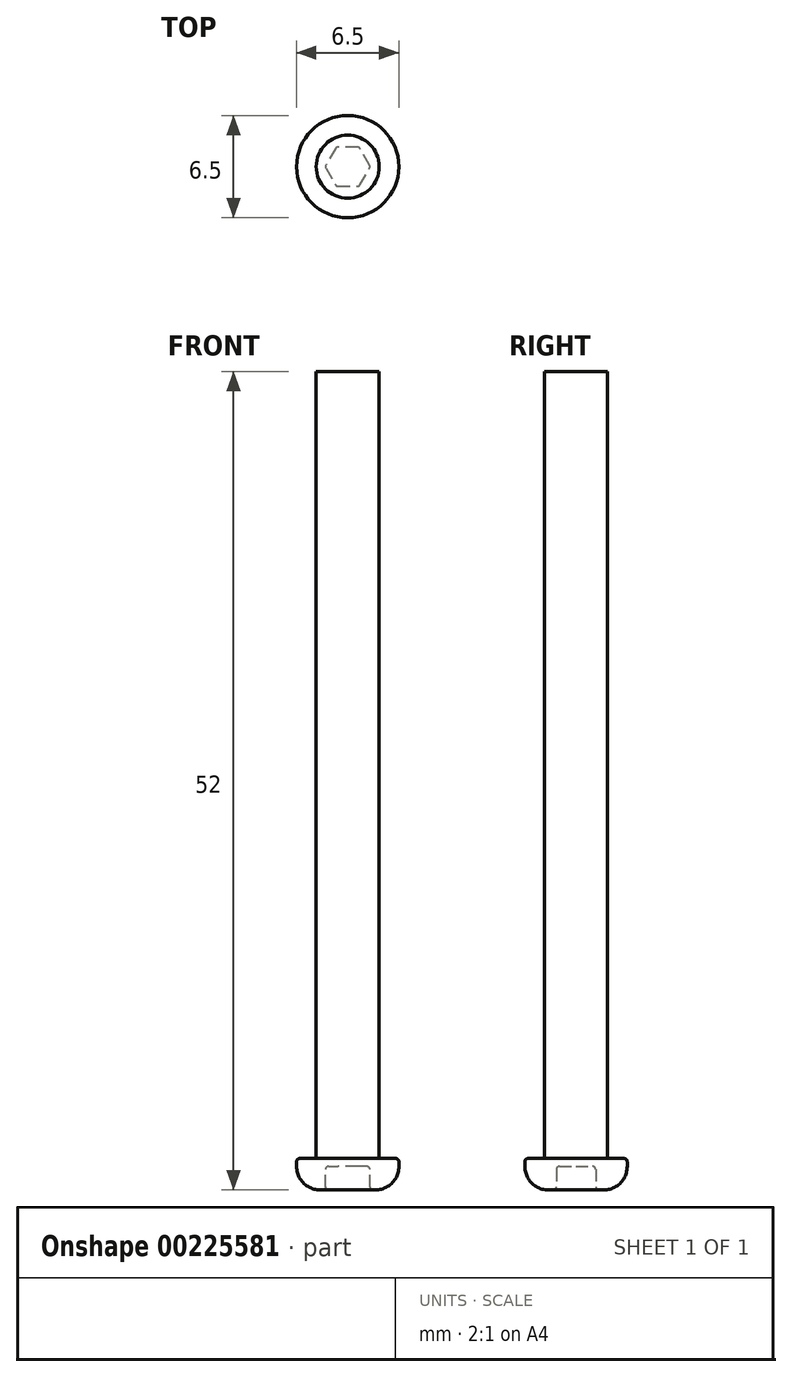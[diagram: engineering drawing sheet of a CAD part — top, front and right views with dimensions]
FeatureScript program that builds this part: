
annotation { "Feature Type Name" : "Feature", "Feature Type Description" : "" }
export const myFeature = defineFeature(function(context is Context, id is Id, definition is map)
    precondition{}
    {
        {
            var Q0;
            Q0=qCreatedBy(makeId("Top.planeOp"),FACE);
            var sketch = newSketch(context, id + "F0", { "sketchPlane" : qUnion([Q0])});
            skCircle(sketch, "E0", {"center": v(0, 0) * mm, "radius": 3.25 * mm});
            skSolve(sketch);
        }
        {
            var Q0;
            Q0=makeQuery(id+"F0.imprint","IMPRINT",FACE,{"disambiguationData":[TD([[makeQuery(id+"F0.imprint","IMPRINT",EDGE,{"derivedFrom":sQuery(id+"F0.wireOp",EDGE,"E0")}),1.0]])]});
            extrude(context, id + "F1", {"entities" : qUnion([Q0]), "depth" : 2 * mm});
        }
        {
            var Q0;
            Q0=makeQuery(id+"F1.opExtrude","CAP_FACE",FACE,{"disambiguationData":[OSD([sQuery(id+"F0.wireOp",EDGE,"E0")])],"isStart":false});
            var sketch = newSketch(context, id + "F2", { "sketchPlane" : qUnion([Q0])});
            skCircle(sketch, "E1", {"center": v(0, 0) * mm, "radius": 2 * mm});
            skSolve(sketch);
        }
        {
            var Q0;
            Q0=makeQuery(id+"F2.imprint","IMPRINT",FACE,{"disambiguationData":[TD([[makeQuery(id+"F2.imprint","IMPRINT",EDGE,{"derivedFrom":sQuery(id+"F2.wireOp",EDGE,"E1")}),1.0]])]});
            extrude(context, id + "F3", {"entities" : qUnion([Q0]), "operationType" : NewBodyOperationType.ADD, "depth" : 50 * mm});
        }
        {
            var Q0;
            Q0=makeQuery(id+"F1.opExtrude","CAP_FACE",FACE,{"disambiguationData":[OSD([sQuery(id+"F0.wireOp",EDGE,"E0")])],"isStart":true});
            var sketch = newSketch(context, id + "F4", { "sketchPlane" : qUnion([Q0])});
            skCircle(sketch, "E2.cCircle", {"center": v(0, 0) * mm, "radius": 1.25 * mm, "construction": true});
            skLineSegment(sketch, "E2.0", {"start": v(-0.72, 1.25) * mm, "end": v(0.72, 1.25) * mm});
            skLineSegment(sketch, "E2.1", {"start": v(0.72, 1.25) * mm, "end": v(1.44, 0) * mm});
            skLineSegment(sketch, "E2.2", {"start": v(1.44, 0) * mm, "end": v(0.72, -1.25) * mm});
            skLineSegment(sketch, "E2.3", {"start": v(0.72, -1.25) * mm, "end": v(-0.72, -1.25) * mm});
            skLineSegment(sketch, "E2.4", {"start": v(-0.72, -1.25) * mm, "end": v(-1.44, 0) * mm});
            skLineSegment(sketch, "E2.5", {"start": v(-1.44, 0) * mm, "end": v(-0.72, 1.25) * mm});
            skPoint(sketch, "E2.0.midPoint", {"position": v(0, 1.25) * mm});
            skSolve(sketch);
        }
        {
            var Q0;
            Q0=makeQuery(id+"F4.imprint","IMPRINT",FACE,{"disambiguationData":[TD([[makeQuery(id+"F4.imprint","IMPRINT",EDGE,{"derivedFrom":sQuery(id+"F4.wireOp",EDGE,"E2.0")}),-1.0]])]});
            extrude(context, id + "F5", {"entities" : qUnion([Q0]), "operationType" : NewBodyOperationType.REMOVE, "oppositeDirection" : true, "depth" : 1.5 * mm});
        }
        {
            var Q0;
            Q0=makeQuery(id+"F1.opExtrude","CAP_EDGE",EDGE,{"disambiguationData":[OSD([sQuery(id+"F0.wireOp",EDGE,"E0")])],"isStart":true});
            fillet(context, id + "F6", {"entities" : qUnion([Q0]), "radius" : 1.5 * mm, "tangentPropagation" : true, "allowEdgeOverflow" : false});
        }
        {
            var Q0;
            Q0=makeQuery(id+"F5.boolean.opBoolean","COPY",EDGE,{"derivedFrom":makeQuery(id+"F5.opExtrude","CAP_EDGE",EDGE,{"disambiguationData":[OSD([sQuery(id+"F4.wireOp",EDGE,"E2.0")])],"isStart":true})});
            var Q1;
            Q1=makeQuery(id+"F5.boolean.opBoolean","COPY",EDGE,{"derivedFrom":makeQuery(id+"F5.opExtrude","SWEPT_EDGE",EDGE,{"disambiguationData":[OSD([sQuery(id+"F4.wireOp",EDGE,"E2.0"),sQuery(id+"F4.wireOp",EDGE,"E2.1")])]})});
            var Q2;
            Q2=makeQuery(id+"F5.boolean.opBoolean","COPY",EDGE,{"derivedFrom":makeQuery(id+"F5.opExtrude","CAP_EDGE",EDGE,{"disambiguationData":[OSD([sQuery(id+"F4.wireOp",EDGE,"E2.1")])],"isStart":true})});
            var Q3;
            Q3=makeQuery(id+"F5.boolean.opBoolean","COPY",EDGE,{"derivedFrom":makeQuery(id+"F5.opExtrude","SWEPT_EDGE",EDGE,{"disambiguationData":[OSD([sQuery(id+"F4.wireOp",EDGE,"E2.1"),sQuery(id+"F4.wireOp",EDGE,"E2.2")])]})});
            var Q4;
            Q4=makeQuery(id+"F5.boolean.opBoolean","COPY",EDGE,{"derivedFrom":makeQuery(id+"F5.opExtrude","SWEPT_EDGE",EDGE,{"disambiguationData":[OSD([sQuery(id+"F4.wireOp",EDGE,"E2.2"),sQuery(id+"F4.wireOp",EDGE,"E2.3")])]})});
            var Q5;
            Q5=makeQuery(id+"F5.boolean.opBoolean","COPY",FACE,{"derivedFrom":makeQuery(id+"F5.opExtrude","SWEPT_FACE",FACE,{"disambiguationData":[OSD([sQuery(id+"F4.wireOp",EDGE,"E2.3")])]})});
            var Q6;
            Q6=makeQuery(id+"F5.boolean.opBoolean","COPY",FACE,{"derivedFrom":makeQuery(id+"F5.opExtrude","SWEPT_FACE",FACE,{"disambiguationData":[OSD([sQuery(id+"F4.wireOp",EDGE,"E2.4")])]})});
            var Q7;
            Q7=makeQuery(id+"F5.boolean.opBoolean","COPY",FACE,{"derivedFrom":makeQuery(id+"F5.opExtrude","SWEPT_FACE",FACE,{"disambiguationData":[OSD([sQuery(id+"F4.wireOp",EDGE,"E2.5")])]})});
            var Q8;
            Q8=makeQuery(id+"F5.boolean.opBoolean","COPY",FACE,{"derivedFrom":makeQuery(id+"F5.opExtrude","SWEPT_FACE",FACE,{"disambiguationData":[OSD([sQuery(id+"F4.wireOp",EDGE,"E2.0")])]})});
            var Q9;
            Q9=makeQuery(id+"F5.boolean.opBoolean","COPY",FACE,{"derivedFrom":makeQuery(id+"F5.opExtrude","SWEPT_FACE",FACE,{"disambiguationData":[OSD([sQuery(id+"F4.wireOp",EDGE,"E2.1")])]})});
            var Q10;
            Q10=makeQuery(id+"F5.boolean.opBoolean","COPY",FACE,{"derivedFrom":makeQuery(id+"F5.opExtrude","SWEPT_FACE",FACE,{"disambiguationData":[OSD([sQuery(id+"F4.wireOp",EDGE,"E2.2")])]})});
            fillet(context, id + "F7", {"entities" : qUnion([Q0, Q1, Q2, Q3, Q4, Q5, Q6, Q7, Q8, Q9, Q10]), "radius" : 0.2 * mm, "tangentPropagation" : true, "allowEdgeOverflow" : false});
        }
        {
            var Q0;
            Q0=makeQuery(id+"F1.opExtrude","CAP_EDGE",EDGE,{"disambiguationData":[OSD([sQuery(id+"F0.wireOp",EDGE,"E0")])],"isStart":false});
            fillet(context, id + "F8", {"entities" : qUnion([Q0]), "radius" : 0.2 * mm, "tangentPropagation" : true, "allowEdgeOverflow" : false});
        }
    });
